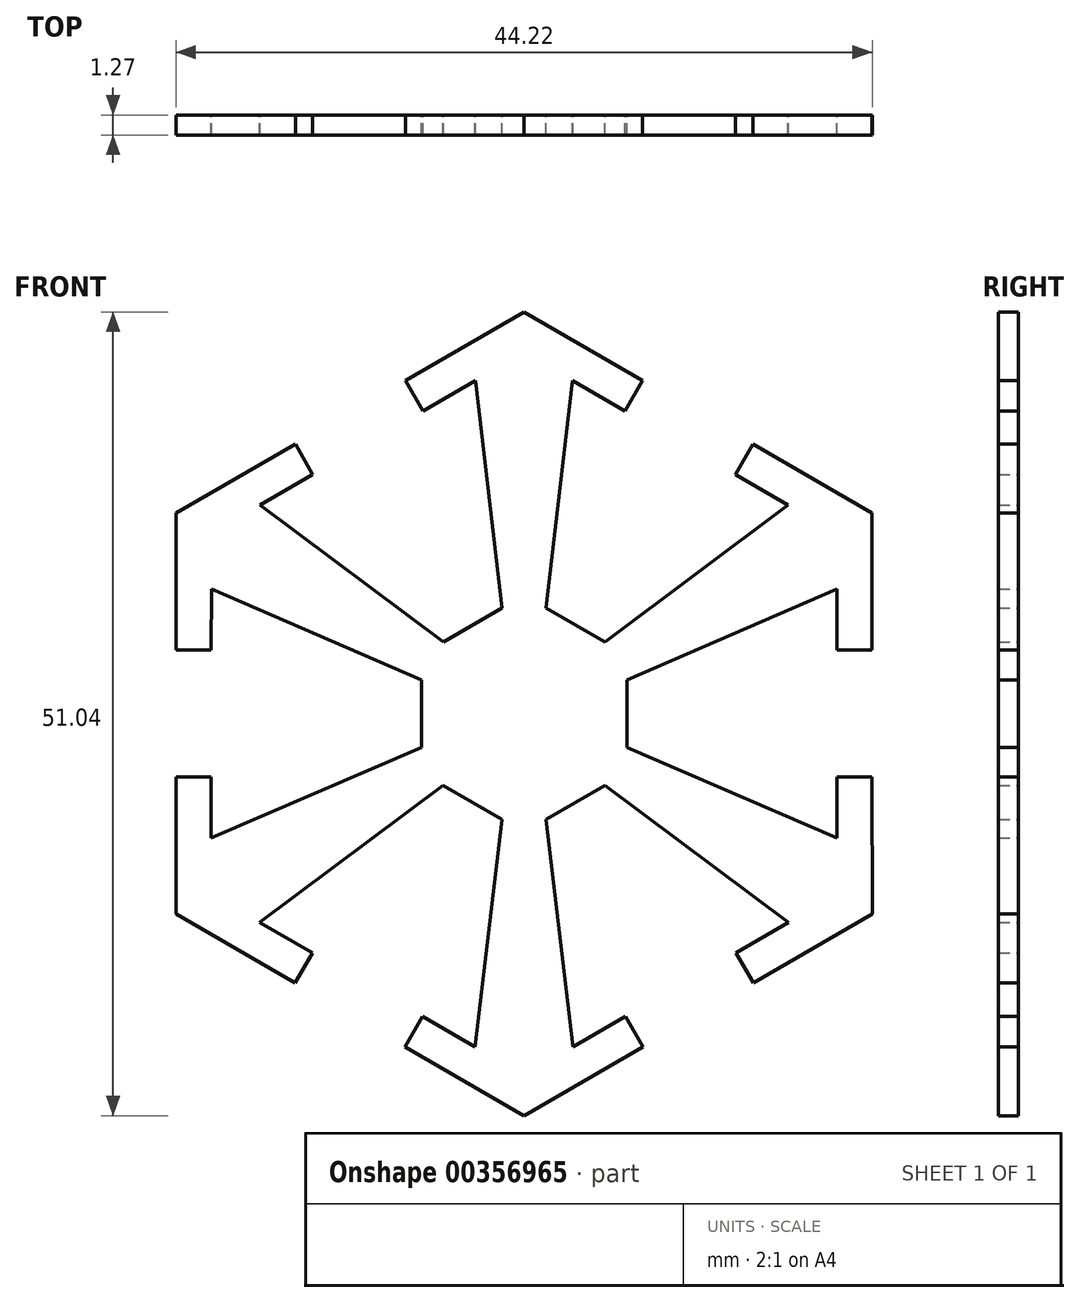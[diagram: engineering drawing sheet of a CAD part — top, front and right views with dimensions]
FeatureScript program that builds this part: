
annotation { "Feature Type Name" : "Feature", "Feature Type Description" : "" }
export const myFeature = defineFeature(function(context is Context, id is Id, definition is map)
    precondition{}
    {
        {
            var Q0;
            Q0=qCreatedBy(makeId("Front.planeOp"),FACE);
            var sketch = newSketch(context, id + "F0", { "sketchPlane" : qUnion([Q0])});
            skCircle(sketch, "E0", {"center": v(-44.64, 40.89) * mm, "radius": 26.63 * mm});
            skLineSegment(sketch, "E1", {"start": v(-44.64, 67.52) * mm, "end": v(-44.64, 14.26) * mm});
            skLineSegment(sketch, "E2.5", {"start": v(-44.64, 66.4) * mm, "end": v(-22.55, 53.64) * mm});
            skPoint(sketch, "E2.0.midPoint", {"position": v(-22.55, 40.89) * mm});
            skPoint(sketch, "E3.0.midPoint", {"position": v(-34.72, 58.1) * mm});
            skPoint(sketch, "E4.0.midPoint", {"position": v(-38.12, 40.89) * mm});
            skLineSegment(sketch, "E5", {"start": v(-43.25, 47.62) * mm, "end": v(-41.57, 62.05) * mm});
            skLineSegment(sketch, "E6", {"start": v(-37.11, 62.05) * mm, "end": v(-38.22, 60.12) * mm});
            skLineSegment(sketch, "E7", {"start": v(-41.57, 62.05) * mm, "end": v(-44.66, 63.83) * mm});
            skLineSegment(sketch, "E8", {"start": v(-39.51, 45.46) * mm, "end": v(-27.88, 54.16) * mm});
            skLineSegment(sketch, "E9", {"start": v(-31.22, 56.09) * mm, "end": v(-30.11, 58) * mm});
            skLineSegment(sketch, "E10", {"start": v(-24.78, 48.8) * mm, "end": v(-38.12, 43.05) * mm});
            skLineSegment(sketch, "E11", {"start": v(-24.78, 44.95) * mm, "end": v(-22.55, 44.95) * mm});
            skLineSegment(sketch, "E12", {"start": v(-44.64, 40.89) * mm, "end": v(-18.02, 40.91) * mm});
            skLineSegment(sketch, "E13", {"start": v(-22.55, 53.64) * mm, "end": v(-22.55, 40.89) * mm});
            skLineSegment(sketch, "E14", {"start": v(-24.78, 52.38) * mm, "end": v(-27.88, 54.16) * mm});
            skLineSegment(sketch, "E15", {"start": v(-27.88, 54.16) * mm, "end": v(-31.22, 56.09) * mm});
            skLineSegment(sketch, "E16", {"start": v(-31.22, 56.09) * mm, "end": v(-38.22, 60.12) * mm});
            skLineSegment(sketch, "E17", {"start": v(-38.22, 60.12) * mm, "end": v(-41.57, 62.05) * mm});
            skLineSegment(sketch, "E18", {"start": v(-24.78, 52.38) * mm, "end": v(-24.78, 48.8) * mm});
            skLineSegment(sketch, "E19", {"start": v(-24.78, 48.8) * mm, "end": v(-24.78, 44.95) * mm});
            skLineSegment(sketch, "E20", {"start": v(-24.78, 44.95) * mm, "end": v(-24.77, 40.9) * mm});
            skPoint(sketch, "E21", {"position": v(-44.64, 48.42) * mm});
            skLineSegment(sketch, "E22", {"start": v(-44.64, 48.42) * mm, "end": v(-43.25, 47.62) * mm});
            skLineSegment(sketch, "E23", {"start": v(-43.25, 47.62) * mm, "end": v(-39.51, 45.46) * mm});
            skLineSegment(sketch, "E24", {"start": v(-39.51, 45.46) * mm, "end": v(-38.12, 44.65) * mm});
            skLineSegment(sketch, "E25", {"start": v(-38.12, 44.65) * mm, "end": v(-38.12, 43.05) * mm});
            skLineSegment(sketch, "E26", {"start": v(-38.12, 43.05) * mm, "end": v(-38.12, 40.89) * mm});
            skLineSegment(sketch, "E27.MirrorCS", {"start": v(-44.6, 15.38) * mm, "end": v(-22.53, 28.17) * mm});
            skLineSegment(sketch, "E28.MirrorCS", {"start": v(-22.53, 28.17) * mm, "end": v(-22.55, 40.93) * mm});
            skLineSegment(sketch, "E29.MirrorCS", {"start": v(-41.53, 19.73) * mm, "end": v(-44.62, 17.95) * mm});
            skLineSegment(sketch, "E30.MirrorCS", {"start": v(-38.2, 21.67) * mm, "end": v(-41.53, 19.73) * mm});
            skLineSegment(sketch, "E31.MirrorCS", {"start": v(-37.08, 19.74) * mm, "end": v(-38.2, 21.67) * mm});
            skLineSegment(sketch, "E32.MirrorCS", {"start": v(-31.2, 25.71) * mm, "end": v(-38.2, 21.67) * mm});
            skLineSegment(sketch, "E33.MirrorCS", {"start": v(-31.2, 25.71) * mm, "end": v(-30.08, 23.8) * mm});
            skLineSegment(sketch, "E34.MirrorCS", {"start": v(-27.85, 27.65) * mm, "end": v(-31.2, 25.71) * mm});
            skLineSegment(sketch, "E35.MirrorCS", {"start": v(-24.76, 29.43) * mm, "end": v(-27.85, 27.65) * mm});
            skLineSegment(sketch, "E36.MirrorCS", {"start": v(-24.76, 29.43) * mm, "end": v(-24.77, 33) * mm});
            skLineSegment(sketch, "E37.MirrorCS", {"start": v(-24.77, 33) * mm, "end": v(-24.77, 36.87) * mm});
            skLineSegment(sketch, "E38.MirrorCS", {"start": v(-24.77, 36.87) * mm, "end": v(-24.77, 40.9) * mm});
            skLineSegment(sketch, "E39.MirrorCS", {"start": v(-24.77, 33) * mm, "end": v(-38.12, 38.74) * mm});
            skLineSegment(sketch, "E40.MirrorCS", {"start": v(-39.5, 36.33) * mm, "end": v(-27.85, 27.65) * mm});
            skLineSegment(sketch, "E41.MirrorCS", {"start": v(-43.24, 34.17) * mm, "end": v(-41.53, 19.73) * mm});
            skLineSegment(sketch, "E42.MirrorCS", {"start": v(-43.24, 34.17) * mm, "end": v(-39.5, 36.33) * mm});
            skPoint(sketch, "E43.MirrorP", {"position": v(-44.63, 33.36) * mm});
            skLineSegment(sketch, "E44.MirrorCS", {"start": v(-44.63, 33.36) * mm, "end": v(-43.24, 34.17) * mm});
            skLineSegment(sketch, "E45.MirrorCS", {"start": v(-39.5, 36.33) * mm, "end": v(-38.12, 37.14) * mm});
            skLineSegment(sketch, "E46.MirrorCS", {"start": v(-38.12, 37.14) * mm, "end": v(-38.12, 38.74) * mm});
            skLineSegment(sketch, "E47.MirrorCS", {"start": v(-38.12, 38.74) * mm, "end": v(-38.12, 40.9) * mm});
            skLineSegment(sketch, "E48.MirrorCS", {"start": v(-51.17, 37.14) * mm, "end": v(-51.17, 38.74) * mm});
            skLineSegment(sketch, "E49.MirrorCS", {"start": v(-49.78, 36.33) * mm, "end": v(-51.17, 37.14) * mm});
            skLineSegment(sketch, "E50.MirrorCS", {"start": v(-51.16, 43.05) * mm, "end": v(-51.16, 40.89) * mm});
            skLineSegment(sketch, "E51.MirrorCS", {"start": v(-49.77, 45.46) * mm, "end": v(-51.16, 44.65) * mm});
            skLineSegment(sketch, "E52.MirrorCS", {"start": v(-51.17, 38.74) * mm, "end": v(-51.16, 40.9) * mm});
            skLineSegment(sketch, "E53.MirrorCS", {"start": v(-51.16, 44.65) * mm, "end": v(-51.16, 43.05) * mm});
            skLineSegment(sketch, "E54.MirrorCS", {"start": v(-64.5, 44.95) * mm, "end": v(-66.73, 44.95) * mm});
            skLineSegment(sketch, "E55.MirrorCS", {"start": v(-52.2, 19.74) * mm, "end": v(-51.1, 21.67) * mm});
            skLineSegment(sketch, "E56.MirrorCS", {"start": v(-58.06, 56.09) * mm, "end": v(-59.17, 58) * mm});
            skLineSegment(sketch, "E57.MirrorCS", {"start": v(-58.09, 25.71) * mm, "end": v(-59.2, 23.8) * mm});
            skLineSegment(sketch, "E58.MirrorCS", {"start": v(-52.17, 62.05) * mm, "end": v(-51.06, 60.12) * mm});
            skLineSegment(sketch, "E59.MirrorCS", {"start": v(-64.52, 33) * mm, "end": v(-64.51, 36.87) * mm});
            skPoint(sketch, "E60.MirrorP", {"position": v(-51.16, 40.89) * mm});
            skLineSegment(sketch, "E61.MirrorCS", {"start": v(-64.5, 44.95) * mm, "end": v(-64.51, 40.9) * mm});
            skLineSegment(sketch, "E62.MirrorCS", {"start": v(-47.75, 19.73) * mm, "end": v(-44.66, 17.95) * mm});
            skLineSegment(sketch, "E63.MirrorCS", {"start": v(-61.43, 27.65) * mm, "end": v(-58.09, 25.71) * mm});
            skLineSegment(sketch, "E64.MirrorCS", {"start": v(-46.04, 34.17) * mm, "end": v(-47.75, 19.73) * mm});
            skLineSegment(sketch, "E65.MirrorCS", {"start": v(-66.75, 28.17) * mm, "end": v(-66.73, 40.93) * mm});
            skLineSegment(sketch, "E66.MirrorCS", {"start": v(-61.4, 54.16) * mm, "end": v(-58.06, 56.09) * mm});
            skLineSegment(sketch, "E67.MirrorCS", {"start": v(-64.51, 36.87) * mm, "end": v(-64.51, 40.9) * mm});
            skLineSegment(sketch, "E68.MirrorCS", {"start": v(-58.06, 56.09) * mm, "end": v(-51.06, 60.12) * mm});
            skLineSegment(sketch, "E69.MirrorCS", {"start": v(-51.06, 60.12) * mm, "end": v(-47.72, 62.05) * mm});
            skLineSegment(sketch, "E70.MirrorCS", {"start": v(-64.52, 29.43) * mm, "end": v(-64.52, 33) * mm});
            skPoint(sketch, "E71.MirrorP", {"position": v(-54.56, 58.1) * mm});
            skLineSegment(sketch, "E72.MirrorCS", {"start": v(-64.5, 48.8) * mm, "end": v(-64.5, 44.95) * mm});
            skLineSegment(sketch, "E73.MirrorCS", {"start": v(-64.5, 48.8) * mm, "end": v(-51.16, 43.05) * mm});
            skLineSegment(sketch, "E74.MirrorCS", {"start": v(-44.64, 40.89) * mm, "end": v(-71.27, 40.91) * mm});
            skLineSegment(sketch, "E75.MirrorCS", {"start": v(-49.77, 45.46) * mm, "end": v(-61.4, 54.16) * mm});
            skPoint(sketch, "E76.MirrorP", {"position": v(-44.65, 33.36) * mm});
            skLineSegment(sketch, "E77.MirrorCS", {"start": v(-49.78, 36.33) * mm, "end": v(-61.43, 27.65) * mm});
            skLineSegment(sketch, "E78.MirrorCS", {"start": v(-46.04, 34.17) * mm, "end": v(-49.78, 36.33) * mm});
            skLineSegment(sketch, "E79.MirrorCS", {"start": v(-46.03, 47.62) * mm, "end": v(-47.72, 62.05) * mm});
            skLineSegment(sketch, "E80.MirrorCS", {"start": v(-64.52, 29.43) * mm, "end": v(-61.43, 27.65) * mm});
            skLineSegment(sketch, "E81.MirrorCS", {"start": v(-44.64, 66.4) * mm, "end": v(-66.73, 53.64) * mm});
            skLineSegment(sketch, "E82.MirrorCS", {"start": v(-66.73, 53.64) * mm, "end": v(-66.73, 40.89) * mm});
            skLineSegment(sketch, "E83.MirrorCS", {"start": v(-51.1, 21.67) * mm, "end": v(-47.75, 19.73) * mm});
            skLineSegment(sketch, "E84.MirrorCS", {"start": v(-47.72, 62.05) * mm, "end": v(-44.62, 63.83) * mm});
            skPoint(sketch, "E85.MirrorP", {"position": v(-66.73, 40.89) * mm});
            skLineSegment(sketch, "E86.MirrorCS", {"start": v(-64.5, 52.38) * mm, "end": v(-64.5, 48.8) * mm});
            skLineSegment(sketch, "E87.MirrorCS", {"start": v(-46.03, 47.62) * mm, "end": v(-49.77, 45.46) * mm});
            skLineSegment(sketch, "E88.MirrorCS", {"start": v(-58.09, 25.71) * mm, "end": v(-51.1, 21.67) * mm});
            skLineSegment(sketch, "E89.MirrorCS", {"start": v(-64.52, 33) * mm, "end": v(-51.17, 38.74) * mm});
            skLineSegment(sketch, "E90.MirrorCS", {"start": v(-44.68, 15.38) * mm, "end": v(-66.75, 28.17) * mm});
            skLineSegment(sketch, "E91.MirrorCS", {"start": v(-64.5, 52.38) * mm, "end": v(-61.4, 54.16) * mm});
            skLineSegment(sketch, "E92.MirrorCS", {"start": v(-44.64, 48.42) * mm, "end": v(-46.03, 47.62) * mm});
            skLineSegment(sketch, "E93.MirrorCS", {"start": v(-44.65, 33.36) * mm, "end": v(-46.04, 34.17) * mm});
            skLineSegment(sketch, "E94.MirrorCS", {"start": v(-24.77, 36.87) * mm, "end": v(-22.54, 36.87) * mm});
            skLineSegment(sketch, "E95.MirrorCS", {"start": v(-64.51, 36.87) * mm, "end": v(-66.74, 36.87) * mm});
            skLineSegment(sketch, "E96", {"start": v(-44.68, 15.38) * mm, "end": v(-44.64, 15.36) * mm});
            skLineSegment(sketch, "E97", {"start": v(-44.64, 15.36) * mm, "end": v(-44.6, 15.38) * mm});
            skLineSegment(sketch, "E98", {"start": v(-44.65, 33.36) * mm, "end": v(-44.64, 33.35) * mm});
            skLineSegment(sketch, "E99", {"start": v(-44.64, 33.35) * mm, "end": v(-44.63, 33.36) * mm});
            skSolve(sketch);
        }
        {
            var Q0;
            Q0=makeQuery(id+"F0.imprint","IMPRINT",FACE,{"disambiguationData":[TD([[makeQuery(id+"F0.imprint","IMPRINT",EDGE,{"derivedFrom":sQuery(id+"F0.wireOp",EDGE,"E42.MirrorCS")}),1.0]])]});
            var Q1;
            {var subQ1=sQuery(id+"F0.wireOp",EDGE,"E48.MirrorCS");Q1=makeQuery(id+"F0.imprint","IMPRINT",FACE,{"disambiguationData":[TD([[makeQuery(id+"F0.imprint","IMPRINT",EDGE,{"derivedFrom":subQ1}),-1.0]])]});}
            var Q2;
            {var subQ0=sQuery(id+"F0.wireOp",EDGE,"E22");Q2=makeQuery(id+"F0.imprint","IMPRINT",FACE,{"disambiguationData":[TD([[makeQuery(id+"F0.imprint","IMPRINT",EDGE,{"derivedFrom":subQ0}),-1.0]])]});}
            var Q3;
            {var subQ1=sQuery(id+"F0.wireOp",EDGE,"E50.MirrorCS");Q3=makeQuery(id+"F0.imprint","IMPRINT",FACE,{"disambiguationData":[TD([[makeQuery(id+"F0.imprint","IMPRINT",EDGE,{"derivedFrom":subQ1}),1.0]])]});}
            var Q4;
            {var subQ4=sQuery(id+"F0.wireOp",EDGE,"E5");Q4=makeQuery(id+"F0.imprint","IMPRINT",FACE,{"disambiguationData":[TD([[makeQuery(id+"F0.imprint","IMPRINT",EDGE,{"derivedFrom":subQ4}),1.0]])]});}
            var Q5;
            {var subQ4=sQuery(id+"F0.wireOp",EDGE,"E79.MirrorCS");Q5=makeQuery(id+"F0.imprint","IMPRINT",FACE,{"disambiguationData":[TD([[makeQuery(id+"F0.imprint","IMPRINT",EDGE,{"derivedFrom":subQ4}),-1.0]])]});}
            var Q6;
            {var subQ6=sQuery(id+"F0.wireOp",EDGE,"E6");Q6=makeQuery(id+"F0.imprint","IMPRINT",FACE,{"disambiguationData":[TD([[makeQuery(id+"F0.imprint","IMPRINT",EDGE,{"derivedFrom":subQ6}),-1.0]])]});}
            var Q7;
            {var subQ3=sQuery(id+"F0.wireOp",EDGE,"E58.MirrorCS");Q7=makeQuery(id+"F0.imprint","IMPRINT",FACE,{"disambiguationData":[TD([[makeQuery(id+"F0.imprint","IMPRINT",EDGE,{"derivedFrom":subQ3}),1.0]])]});}
            var Q8;
            {var subQ6=sQuery(id+"F0.wireOp",EDGE,"E9");Q8=makeQuery(id+"F0.imprint","IMPRINT",FACE,{"disambiguationData":[TD([[makeQuery(id+"F0.imprint","IMPRINT",EDGE,{"derivedFrom":subQ6}),-1.0]])]});}
            var Q9;
            Q9=makeQuery(id+"F0.imprint","IMPRINT",FACE,{"disambiguationData":[TD([[makeQuery(id+"F0.imprint","IMPRINT",EDGE,{"derivedFrom":sQuery(id+"F0.wireOp",EDGE,"E8")}),-1.0]])]});
            var Q10;
            {var subQ0=sQuery(id+"F0.wireOp",EDGE,"E33.MirrorCS");Q10=makeQuery(id+"F0.imprint","IMPRINT",FACE,{"disambiguationData":[TD([[makeQuery(id+"F0.imprint","IMPRINT",EDGE,{"derivedFrom":subQ0}),1.0]])]});}
            var Q11;
            Q11=makeQuery(id+"F0.imprint","IMPRINT",FACE,{"disambiguationData":[TD([[makeQuery(id+"F0.imprint","IMPRINT",EDGE,{"derivedFrom":sQuery(id+"F0.wireOp",EDGE,"E35.MirrorCS")}),-1.0]])]});
            var Q12;
            {var subQ1=sQuery(id+"F0.wireOp",EDGE,"E55.MirrorCS");Q12=makeQuery(id+"F0.imprint","IMPRINT",FACE,{"disambiguationData":[TD([[makeQuery(id+"F0.imprint","IMPRINT",EDGE,{"derivedFrom":subQ1}),-1.0]])]});}
            var Q13;
            Q13=makeQuery(id+"F0.imprint","IMPRINT",FACE,{"disambiguationData":[TD([[makeQuery(id+"F0.imprint","IMPRINT",EDGE,{"derivedFrom":sQuery(id+"F0.wireOp",EDGE,"E30.MirrorCS")}),1.0]])]});
            var Q14;
            Q14=makeQuery(id+"F0.imprint","IMPRINT",FACE,{"disambiguationData":[TD([[makeQuery(id+"F0.imprint","IMPRINT",EDGE,{"derivedFrom":sQuery(id+"F0.wireOp",EDGE,"E48.MirrorCS")}),1.0]])]});
            var Q15;
            {var subQ6=sQuery(id+"F0.wireOp",EDGE,"E57.MirrorCS");Q15=makeQuery(id+"F0.imprint","IMPRINT",FACE,{"disambiguationData":[TD([[makeQuery(id+"F0.imprint","IMPRINT",EDGE,{"derivedFrom":subQ6}),-1.0]])]});}
            var Q16;
            Q16=makeQuery(id+"F0.imprint","IMPRINT",FACE,{"disambiguationData":[TD([[makeQuery(id+"F0.imprint","IMPRINT",EDGE,{"derivedFrom":sQuery(id+"F0.wireOp",EDGE,"E51.MirrorCS")}),-1.0]])]});
            var Q17;
            {var subQ5=sQuery(id+"F0.wireOp",EDGE,"E56.MirrorCS");Q17=makeQuery(id+"F0.imprint","IMPRINT",FACE,{"disambiguationData":[TD([[makeQuery(id+"F0.imprint","IMPRINT",EDGE,{"derivedFrom":subQ5}),1.0]])]});}
            extrude(context, id + "F1", {"entities" : qUnion([Q0, Q1, Q2, Q3, Q4, Q5, Q6, Q7, Q8, Q9, Q10, Q11, Q12, Q13, Q14, Q15, Q16, Q17]), "depth" : 1.27 * mm});
        }
    });
